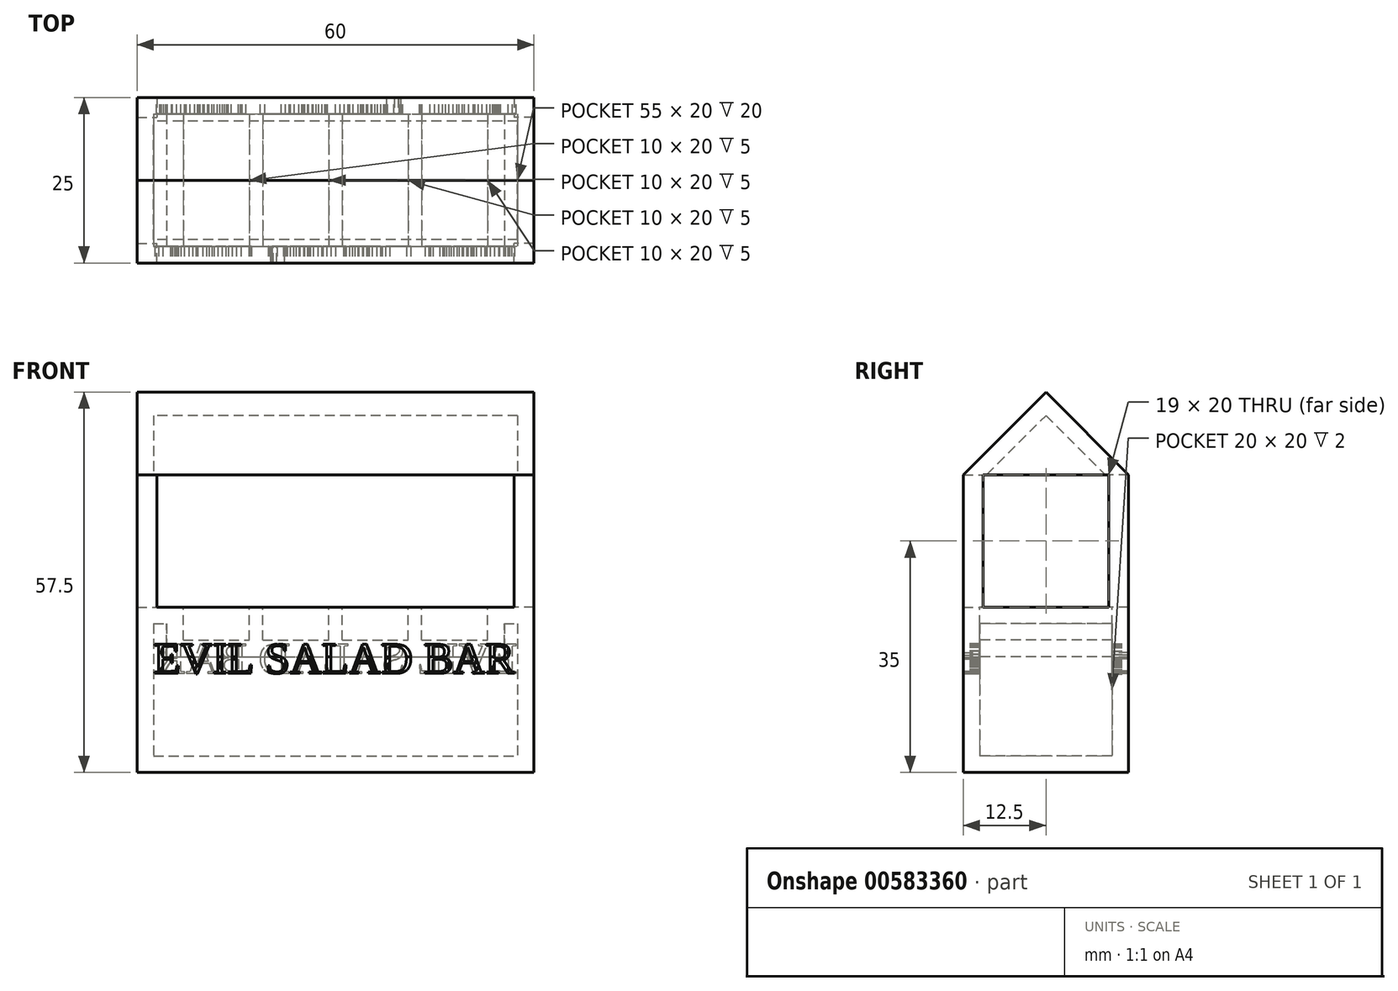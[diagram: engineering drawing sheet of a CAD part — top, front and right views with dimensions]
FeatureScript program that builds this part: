
annotation { "Feature Type Name" : "Feature", "Feature Type Description" : "" }
export const myFeature = defineFeature(function(context is Context, id is Id, definition is map)
    precondition{}
    {
        {
            var Q0;
            Q0=qCreatedBy(makeId("Top.planeOp"),FACE);
            var sketch = newSketch(context, id + "F0", { "sketchPlane" : qUnion([Q0])});
            skLineSegment(sketch, "E0.bottom", {"start": v(-58.32, 8.65) * mm, "end": v(1.68, 8.65) * mm});
            skLineSegment(sketch, "E0.top", {"start": v(-58.32, -16.35) * mm, "end": v(1.68, -16.35) * mm});
            skLineSegment(sketch, "E0.left", {"start": v(-58.32, 8.65) * mm, "end": v(-58.32, -16.35) * mm});
            skLineSegment(sketch, "E0.right", {"start": v(1.68, 8.65) * mm, "end": v(1.68, -16.35) * mm});
            skSolve(sketch);
        }
        {
            var Q0;
            Q0=makeQuery(id+"F0.imprint","IMPRINT",FACE,{"disambiguationData":[TD([[makeQuery(id+"F0.imprint","IMPRINT",EDGE,{"derivedFrom":sQuery(id+"F0.wireOp",EDGE,"E0.bottom")}),-1.0]])]});
            extrude(context, id + "F1", {"entities" : qUnion([Q0]), "depth" : 25 * mm, "offsetDistance" : 25 * mm});
        }
        {
            var Q0;
            Q0=makeQuery(id+"F1.opExtrude","CAP_FACE",FACE,{"disambiguationData":[OSD([sQuery(id+"F0.wireOp",EDGE,"E0.bottom"),sQuery(id+"F0.wireOp",EDGE,"E0.top"),sQuery(id+"F0.wireOp",EDGE,"E0.left"),sQuery(id+"F0.wireOp",EDGE,"E0.right")])],"isStart":false});
            var sketch = newSketch(context, id + "F2", { "sketchPlane" : qUnion([Q0])});
            skLineSegment(sketch, "E1.bottom", {"start": v(-51.32, 6.15) * mm, "end": v(-41.32, 6.15) * mm});
            skLineSegment(sketch, "E1.top", {"start": v(-51.32, -13.85) * mm, "end": v(-41.32, -13.85) * mm});
            skLineSegment(sketch, "E1.left", {"start": v(-51.32, 6.15) * mm, "end": v(-51.32, -13.85) * mm});
            skLineSegment(sketch, "E1.right", {"start": v(-41.32, 6.15) * mm, "end": v(-41.32, -13.85) * mm});
            skLineSegment(sketch, "E2.bottom", {"start": v(-39.32, 6.15) * mm, "end": v(-29.32, 6.15) * mm});
            skLineSegment(sketch, "E2.top", {"start": v(-39.32, -13.85) * mm, "end": v(-29.32, -13.85) * mm});
            skLineSegment(sketch, "E2.left", {"start": v(-39.32, 6.15) * mm, "end": v(-39.32, -13.85) * mm});
            skLineSegment(sketch, "E2.right", {"start": v(-29.32, 6.15) * mm, "end": v(-29.32, -13.85) * mm});
            skLineSegment(sketch, "E3.bottom", {"start": v(-27.32, 6.15) * mm, "end": v(-17.32, 6.15) * mm});
            skLineSegment(sketch, "E3.top", {"start": v(-27.32, -13.85) * mm, "end": v(-17.32, -13.85) * mm});
            skLineSegment(sketch, "E3.left", {"start": v(-27.32, 6.15) * mm, "end": v(-27.32, -13.85) * mm});
            skLineSegment(sketch, "E3.right", {"start": v(-17.32, 6.15) * mm, "end": v(-17.32, -13.85) * mm});
            skLineSegment(sketch, "E4.bottom", {"start": v(-15.32, 6.15) * mm, "end": v(-5.32, 6.15) * mm});
            skLineSegment(sketch, "E4.top", {"start": v(-15.32, -13.85) * mm, "end": v(-5.32, -13.85) * mm});
            skLineSegment(sketch, "E4.left", {"start": v(-15.32, 6.15) * mm, "end": v(-15.32, -13.85) * mm});
            skLineSegment(sketch, "E4.right", {"start": v(-5.32, 6.15) * mm, "end": v(-5.32, -13.85) * mm});
            skSolve(sketch);
        }
        {
            var Q0;
            Q0=makeQuery(id+"F2.imprint","IMPRINT",FACE,{"disambiguationData":[TD([[makeQuery(id+"F2.imprint","IMPRINT",EDGE,{"derivedFrom":sQuery(id+"F2.wireOp",EDGE,"E1.bottom")}),-1.0]])]});
            var Q1;
            Q1=makeQuery(id+"F2.imprint","IMPRINT",FACE,{"disambiguationData":[TD([[makeQuery(id+"F2.imprint","IMPRINT",EDGE,{"derivedFrom":sQuery(id+"F2.wireOp",EDGE,"E2.bottom")}),-1.0]])]});
            var Q2;
            Q2=makeQuery(id+"F2.imprint","IMPRINT",FACE,{"disambiguationData":[TD([[makeQuery(id+"F2.imprint","IMPRINT",EDGE,{"derivedFrom":sQuery(id+"F2.wireOp",EDGE,"E3.bottom")}),-1.0]])]});
            var Q3;
            Q3=makeQuery(id+"F2.imprint","IMPRINT",FACE,{"disambiguationData":[TD([[makeQuery(id+"F2.imprint","IMPRINT",EDGE,{"derivedFrom":sQuery(id+"F2.wireOp",EDGE,"E4.bottom")}),-1.0]])]});
            extrude(context, id + "F3", {"entities" : qUnion([Q0, Q1, Q2, Q3]), "operationType" : NewBodyOperationType.REMOVE, "oppositeDirection" : true, "depth" : 5 * mm, "offsetDistance" : 25 * mm});
        }
        {
            var Q0;
            Q0=makeQuery(id+"F1.opExtrude","CAP_FACE",FACE,{"disambiguationData":[OSD([sQuery(id+"F0.wireOp",EDGE,"E0.bottom"),sQuery(id+"F0.wireOp",EDGE,"E0.top"),sQuery(id+"F0.wireOp",EDGE,"E0.left"),sQuery(id+"F0.wireOp",EDGE,"E0.right")])],"isStart":false});
            var sketch = newSketch(context, id + "F4", { "sketchPlane" : qUnion([Q0])});
            skLineSegment(sketch, "E5.bottom", {"start": v(1.68, -16.35) * mm, "end": v(-1.32, -16.35) * mm});
            skLineSegment(sketch, "E5.top", {"start": v(1.68, -13.35) * mm, "end": v(-1.32, -13.35) * mm});
            skLineSegment(sketch, "E5.left", {"start": v(1.68, -16.35) * mm, "end": v(1.68, -13.35) * mm});
            skLineSegment(sketch, "E5.right", {"start": v(-1.32, -16.35) * mm, "end": v(-1.32, -13.35) * mm});
            skLineSegment(sketch, "E6.bottom", {"start": v(1.68, 8.65) * mm, "end": v(-1.32, 8.65) * mm});
            skLineSegment(sketch, "E6.top", {"start": v(1.68, 5.65) * mm, "end": v(-1.32, 5.65) * mm});
            skLineSegment(sketch, "E6.left", {"start": v(1.68, 8.65) * mm, "end": v(1.68, 5.65) * mm});
            skLineSegment(sketch, "E6.right", {"start": v(-1.32, 8.65) * mm, "end": v(-1.32, 5.65) * mm});
            skLineSegment(sketch, "E7.bottom", {"start": v(-58.32, 8.65) * mm, "end": v(-55.32, 8.65) * mm});
            skLineSegment(sketch, "E7.top", {"start": v(-58.32, 5.65) * mm, "end": v(-55.32, 5.65) * mm});
            skLineSegment(sketch, "E7.left", {"start": v(-58.32, 8.65) * mm, "end": v(-58.32, 5.65) * mm});
            skLineSegment(sketch, "E7.right", {"start": v(-55.32, 8.65) * mm, "end": v(-55.32, 5.65) * mm});
            skLineSegment(sketch, "E8.bottom", {"start": v(-58.32, -16.35) * mm, "end": v(-55.32, -16.35) * mm});
            skLineSegment(sketch, "E8.top", {"start": v(-58.32, -13.35) * mm, "end": v(-55.32, -13.35) * mm});
            skLineSegment(sketch, "E8.left", {"start": v(-58.32, -16.35) * mm, "end": v(-58.32, -13.35) * mm});
            skLineSegment(sketch, "E8.right", {"start": v(-55.32, -16.35) * mm, "end": v(-55.32, -13.35) * mm});
            skSolve(sketch);
        }
        {
            var Q0;
            Q0 = qSketchRegion(id + "F4", true);
            extrude(context, id + "F5", {"entities" : qUnion([Q0]), "operationType" : NewBodyOperationType.ADD, "depth" : 20 * mm, "offsetDistance" : 25 * mm});
        }
        {
            var Q0;
            Q0=makeQuery(id+"F5.boolean.opBoolean","MERGE",FACE,{"derivedFrom":[makeQuery(id+"F1.opExtrude","SWEPT_FACE",FACE,{"disambiguationData":[OSD([sQuery(id+"F0.wireOp",EDGE,"E0.left")])]}),makeQuery(id+"F5.opExtrude","SWEPT_FACE",FACE,{"disambiguationData":[OSD([sQuery(id+"F4.wireOp",EDGE,"E7.left")])]}),makeQuery(id+"F5.opExtrude","SWEPT_FACE",FACE,{"disambiguationData":[OSD([sQuery(id+"F4.wireOp",EDGE,"E8.left")])]})]});
            var sketch = newSketch(context, id + "F6", { "sketchPlane" : qUnion([Q0])});
            skLineSegment(sketch, "E9", {"start": v(-8.65, 45) * mm, "end": v(16.35, 45) * mm});
            skLineSegment(sketch, "E10", {"start": v(16.35, 45) * mm, "end": v(3.85, 57.5) * mm});
            skPoint(sketch, "E10.endSnap0", {"position": v(3.85, 45) * mm});
            skLineSegment(sketch, "E11", {"start": v(3.85, 57.5) * mm, "end": v(-8.65, 45) * mm});
            skSolve(sketch);
        }
        {
            var Q0;
            Q0 = qSketchRegion(id + "F6", true);
            extrude(context, id + "F7", {"entities" : qUnion([Q0]), "operationType" : NewBodyOperationType.ADD, "oppositeDirection" : true, "depth" : 60 * mm, "offsetDistance" : 25 * mm});
        }
        {
            var Q0;
            Q0=makeQuery(id+"F7.opExtrude","SWEPT_FACE",FACE,{"disambiguationData":[OSD([sQuery(id+"F6.wireOp",EDGE,"E9")])]});
            shell(context, id + "F8", {"entities" : qUnion([Q0]), "thickness" : 2.5 * mm});
        }
        {
            var Q0;
            Q0=makeQuery(id+"F5.boolean.opBoolean","MERGE",FACE,{"derivedFrom":[makeQuery(id+"F1.opExtrude","SWEPT_FACE",FACE,{"disambiguationData":[OSD([sQuery(id+"F0.wireOp",EDGE,"E0.top")])]}),makeQuery(id+"F5.opExtrude","SWEPT_FACE",FACE,{"disambiguationData":[OSD([sQuery(id+"F4.wireOp",EDGE,"E5.bottom")])]}),makeQuery(id+"F5.opExtrude","SWEPT_FACE",FACE,{"disambiguationData":[OSD([sQuery(id+"F4.wireOp",EDGE,"E8.bottom")])]})]});
            var sketch = newSketch(context, id + "F9", { "sketchPlane" : qUnion([Q0])});
            skText(sketch, "E12", { "text": "EVIL SALAD BAR", "fontName": "Tinos-Regular.ttf"});
            const initialGuessF9  = {"E12": [-0.05582, 0.015, 1, 0, 0.00481]};
            skSetInitialGuess(sketch, initialGuessF9);
            skSolve(sketch);
        }
        {
            var Q0;
            Q0 = qSketchRegion(id + "F9", true);
            extrude(context, id + "F10", {"entities" : qUnion([Q0]), "operationType" : NewBodyOperationType.REMOVE, "oppositeDirection" : true, "depth" : 2.5 * mm, "offsetDistance" : 25 * mm});
        }
        {
            var Q0;
            Q0=makeQuery(id+"F5.boolean.opBoolean","MERGE",FACE,{"derivedFrom":[makeQuery(id+"F1.opExtrude","SWEPT_FACE",FACE,{"disambiguationData":[OSD([sQuery(id+"F0.wireOp",EDGE,"E0.bottom")])]}),makeQuery(id+"F5.opExtrude","SWEPT_FACE",FACE,{"disambiguationData":[OSD([sQuery(id+"F4.wireOp",EDGE,"E6.bottom")])]}),makeQuery(id+"F5.opExtrude","SWEPT_FACE",FACE,{"disambiguationData":[OSD([sQuery(id+"F4.wireOp",EDGE,"E7.bottom")])]})]});
            var sketch = newSketch(context, id + "F11", { "sketchPlane" : qUnion([Q0])});
            skText(sketch, "E13", { "text": "EVIL SALAD BAR", "fontName": "Tinos-Regular.ttf"});
            const initialGuessF11  = {"E13": [0.00082, 0.015, 1, 0, 0.00481]};
            skSetInitialGuess(sketch, initialGuessF11);
            skSolve(sketch);
        }
        {
            var Q0;
            Q0 = qSketchRegion(id + "F11", true);
            extrude(context, id + "F12", {"entities" : qUnion([Q0]), "operationType" : NewBodyOperationType.REMOVE, "oppositeDirection" : true, "depth" : 2.5 * mm, "offsetDistance" : 25 * mm});
        }
    });
